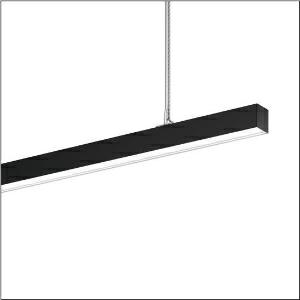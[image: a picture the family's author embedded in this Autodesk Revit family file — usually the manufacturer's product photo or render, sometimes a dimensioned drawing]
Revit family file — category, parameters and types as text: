
# Revit family: silica_r__21_51mx33dc4dbb_4870
name_source: partatom
category: Lighting Fixtures
units: mm (PartAtom-declared; Revit-internal decimal feet)

## family parameters
Cut with Voids When Loaded = No
Host = Face
Light Source = No
Part Type = Normal
Room Calculation Point = No
Round Connector Dimension = Use Diameter
Shared = No

## types (1)
- --- (1 x LED, 14790 lm, 93.9 W, 4000K)
    Apparent Load = 94 VA
    CIE Flux Codes = 78 96 99 55 100
    Color Rendering = 80
    Color Temperature = 4000K
    Default Elevation = 1800 mm
    Description = Silica® 21, office luminaire, primary optical cover: prismatic diffuser, of PMMA, CAT 2 (L<= 3000cd/m²), light emission: direct/indirect distribution, primary light characteristic: symmetric, installation type: suspended mounting, LED, rated luminous flux: 14.790lm, luminous efficacy: 158lm/W, light colour: 840, colour temperature: 4000K, with terminal, 3+2-pole, max. 2.5mm², mains connection: 220..240V, AC, 50/60Hz, rated input power: 93.9W, luminaire housing, of aluminium, jet black (RAL 9005), length: 3.004mm, width: 53mm, height: 53mm, protection rating (complete): IP20, insulation class (complete): insulation class I (protective earthing), certification: CE, permissible operating ambient temperature: 0..+35°C, standard: EN 50419, packaging unit: 1 piece
    Height = 53 mm
    Lamp = 1 x LED
    Lamp Light Flux = 14790 lm
    Lamp Power = 93.9 W
    Lamp count = 1
    Length = 3004 mm
    Luminous efficacy = 158 lm/W
    Manufacturer = Siteco
    ModVariant = No
    Model = 51MX33DC4DBB
    Mounting Place = Ceiling
    Mounting Type = Pendant
    Number of Poles = 1
    OnlyDefault = Yes
    Power Factor = 1
    Product Name = Silica® 21
    Product group = office luminaire | ceiling pendant
    ProductGroupID = 902
    Protection Class = Protection class I
    Protection Degree = IP 20
    RLX_Detail_Level = 1
    RLX_Emergency_Light_Flux = 0 lm
    RLX_Emergency_Type = 0
    RLX_Emergency_Type_DB = No
    RlxData = <blob elided: 26041 chars, md5=5dc56bda>
    Socket = socket
    Standby Power = 0 W
    System Light Flux = 14790 lm
    System Power = 94 W
    Type Comments = factory setting: luminous flux: 100 % | dim-lin: 254 | 323 mA
    Type Image = l_1297744.jpg
    URL = http://relux.com
    VarID = @adj_049029
    Voltage = 0 V
    Weight = 0.00 kg
    Width = 53 mm

## geometry (parser evidence)
native form markers: Blend x4, Sweep x14
no freeform markers — native parametric forms only
